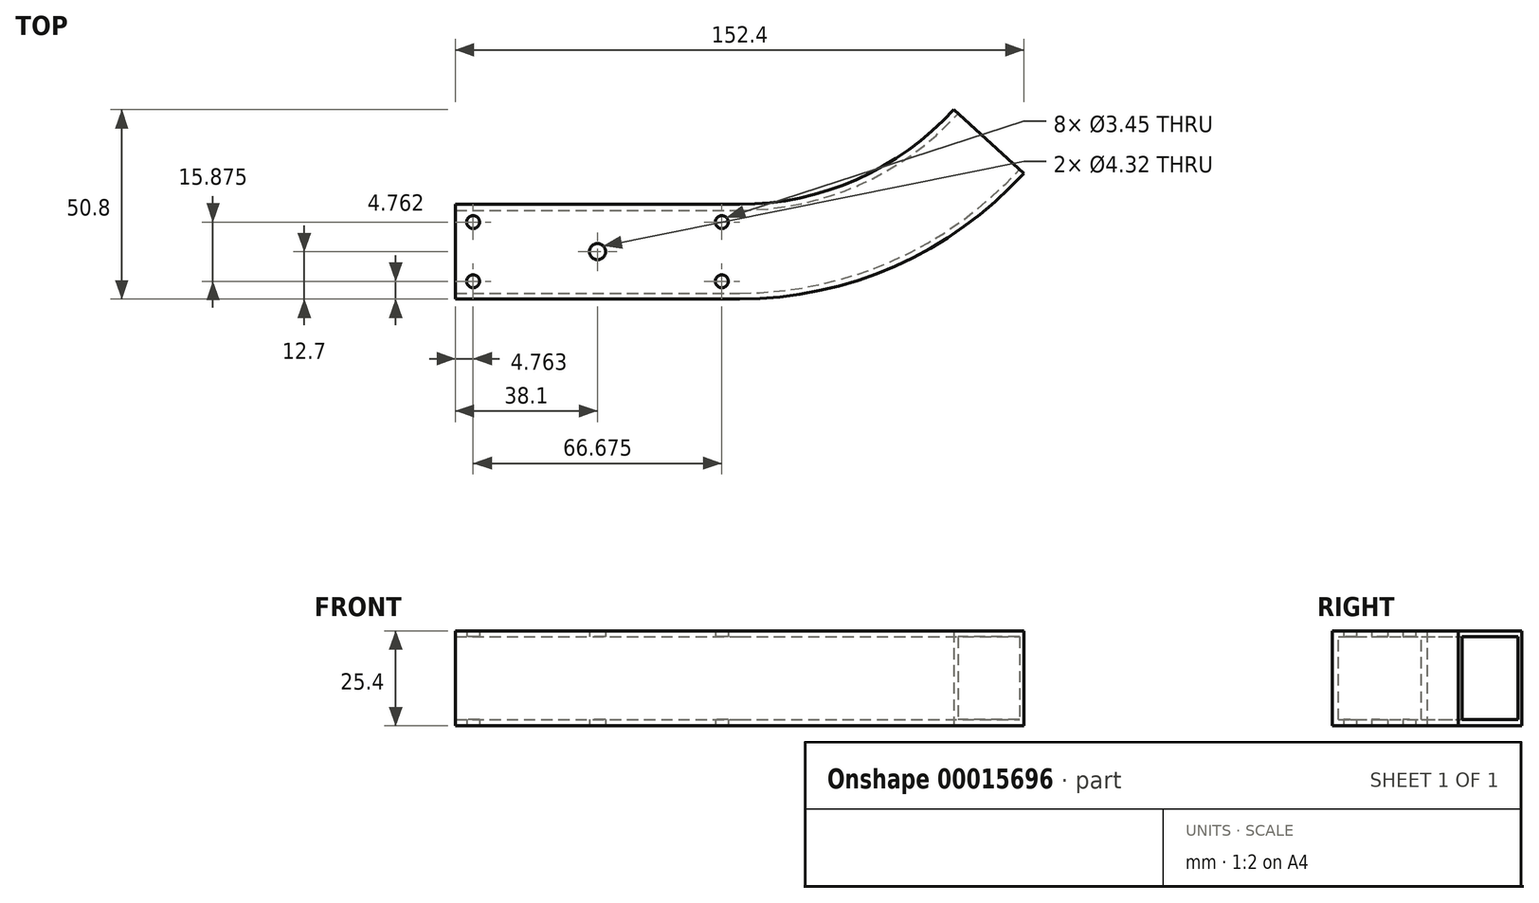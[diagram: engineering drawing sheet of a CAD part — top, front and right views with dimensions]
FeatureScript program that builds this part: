
annotation { "Feature Type Name" : "Feature", "Feature Type Description" : "" }
export const myFeature = defineFeature(function(context is Context, id is Id, definition is map)
    precondition{}
    {
        {
            var Q0;
            Q0=qCreatedBy(makeId("Top.planeOp"),FACE);
            var sketch = newSketch(context, id + "F0", { "sketchPlane" : qUnion([Q0])});
            skLineSegment(sketch, "E0.bottom", {"start": v(0, 0) * mm, "end": v(76.2, 0) * mm});
            skLineSegment(sketch, "E0.top", {"start": v(0, -25.4) * mm, "end": v(76.2, -25.4) * mm});
            skLineSegment(sketch, "E0.left", {"start": v(0, 0) * mm, "end": v(0, -25.4) * mm});
            skLineSegment(sketch, "E0.right", {"start": v(76.2, 0) * mm, "end": v(76.2, -25.4) * mm});
            skArc(sketch, "E1", {"start": v(76.2, 0) * mm, "mid": v(107.59, 6.63) * mm, "end": v(133.6, 25.4) * mm});
            skArc(sketch, "E2", {"start": v(76.2, -25.4) * mm, "mid": v(117.86, -16.6) * mm, "end": v(152.4, 8.32) * mm});
            skLineSegment(sketch, "E3", {"start": v(152.4, 8.32) * mm, "end": v(133.6, 25.4) * mm});
            skLineSegment(sketch, "E4", {"start": v(76.2, 0) * mm, "end": v(76.2, 77.56) * mm, "construction": true});
            skLineSegment(sketch, "E5", {"start": v(76.2, 77.56) * mm, "end": v(133.6, 25.4) * mm, "construction": true});
            skSolve(sketch);
        }
        {
            var Q0;
            Q0 = qSketchRegion(id + "F0", true);
            extrude(context, id + "F1", {"entities" : qUnion([Q0]), "depth" : 25.4 * mm});
        }
        {
            var Q0;
            Q0=makeQuery(id+"F1.opExtrude","SWEPT_FACE",FACE,{"disambiguationData":[OSD([sQuery(id+"F0.wireOp",EDGE,"E3")])]});
            shell(context, id + "F2", {"entities" : qUnion([Q0]), "thickness" : 1.59 * mm});
        }
        {
            var Q0;
            Q0=makeQuery(id+"F1.opExtrude","SWEPT_FACE",FACE,{"disambiguationData":[OSD([sQuery(id+"F0.wireOp",EDGE,"E0.left")])]});
            var sketch = newSketch(context, id + "F3", { "sketchPlane" : qUnion([Q0])});
            skLineSegment(sketch, "E6.rect.bottom", {"start": v(23.81, 1.59) * mm, "end": v(1.59, 1.59) * mm});
            skLineSegment(sketch, "E6.rect.top", {"start": v(23.81, 23.81) * mm, "end": v(1.59, 23.81) * mm});
            skLineSegment(sketch, "E6.rect.left", {"start": v(23.81, 1.59) * mm, "end": v(23.81, 23.81) * mm});
            skLineSegment(sketch, "E6.rect.right", {"start": v(1.59, 1.59) * mm, "end": v(1.59, 23.81) * mm});
            skPoint(sketch, "E6.rect.middle", {"position": v(12.7, 12.7) * mm});
            skLineSegment(sketch, "E7", {"start": v(0, 12.7) * mm, "end": v(25.4, 12.7) * mm, "construction": true});
            skSolve(sketch);
        }
        {
            var Q0;
            Q0 = qSketchRegion(id + "F3", true);
            extrude(context, id + "F4", {"entities" : qUnion([Q0]), "operationType" : NewBodyOperationType.REMOVE, "oppositeDirection" : true, "depth" : 1.59 * mm});
        }
        {
            var Q0;
            Q0=makeQuery(id+"F1.opExtrude","CAP_FACE",FACE,{"disambiguationData":[OSD([sQuery(id+"F0.wireOp",EDGE,"E0.bottom"),sQuery(id+"F0.wireOp",EDGE,"E0.top"),sQuery(id+"F0.wireOp",EDGE,"E0.left"),sQuery(id+"F0.wireOp",EDGE,"E1"),sQuery(id+"F0.wireOp",EDGE,"E2"),sQuery(id+"F0.wireOp",EDGE,"E3")])],"isStart":true});
            var sketch = newSketch(context, id + "F5", { "sketchPlane" : qUnion([Q0])});
            skLineSegment(sketch, "E8", {"start": v(38.1, 0) * mm, "end": v(38.1, 25.4) * mm, "construction": true});
            skLineSegment(sketch, "E9", {"start": v(4.76, 0) * mm, "end": v(4.76, 4.76) * mm, "construction": true});
            skLineSegment(sketch, "E10", {"start": v(4.76, 4.76) * mm, "end": v(0, 4.76) * mm, "construction": true});
            skLineSegment(sketch, "E11", {"start": v(4.76, 4.76) * mm, "end": v(4.76, 20.64) * mm, "construction": true});
            skLineSegment(sketch, "E12", {"start": v(4.76, 20.64) * mm, "end": v(4.76, 25.4) * mm, "construction": true});
            skLineSegment(sketch, "E13", {"start": v(76.2, 0) * mm, "end": v(76.2, 25.4) * mm, "construction": true});
            skLineSegment(sketch, "E14", {"start": v(76.2, 4.76) * mm, "end": v(71.44, 4.76) * mm, "construction": true});
            skLineSegment(sketch, "E15", {"start": v(71.44, 4.76) * mm, "end": v(71.44, 0) * mm, "construction": true});
            skLineSegment(sketch, "E16", {"start": v(71.44, 4.76) * mm, "end": v(71.44, 20.64) * mm, "construction": true});
            skCircle(sketch, "E17", {"center": v(71.44, 4.76) * mm, "radius": 1.73 * mm});
            skCircle(sketch, "E18", {"center": v(71.44, 20.64) * mm, "radius": 1.73 * mm});
            skCircle(sketch, "E19", {"center": v(4.76, 4.76) * mm, "radius": 1.73 * mm});
            skCircle(sketch, "E20", {"center": v(4.76, 20.64) * mm, "radius": 1.73 * mm});
            skCircle(sketch, "E21", {"center": v(38.1, 12.7) * mm, "radius": 2.16 * mm});
            skSolve(sketch);
        }
        {
            var Q0;
            Q0 = qSketchRegion(id + "F5", true);
            var Q1;
            Q1=makeQuery(id+"F1.opExtrude","CAP_FACE",FACE,{"disambiguationData":[OSD([sQuery(id+"F0.wireOp",EDGE,"E0.bottom"),sQuery(id+"F0.wireOp",EDGE,"E0.top"),sQuery(id+"F0.wireOp",EDGE,"E0.left"),sQuery(id+"F0.wireOp",EDGE,"E1"),sQuery(id+"F0.wireOp",EDGE,"E2"),sQuery(id+"F0.wireOp",EDGE,"E3")])],"isStart":false});
            extrude(context, id + "F6", {"entities" : qUnion([Q0]), "operationType" : NewBodyOperationType.REMOVE, "endBound" : BoundingType.UP_TO_SURFACE, "oppositeDirection" : true, "endBoundEntityFace" : qUnion([Q1]), "depth" : 25.4 * mm});
        }
    });
